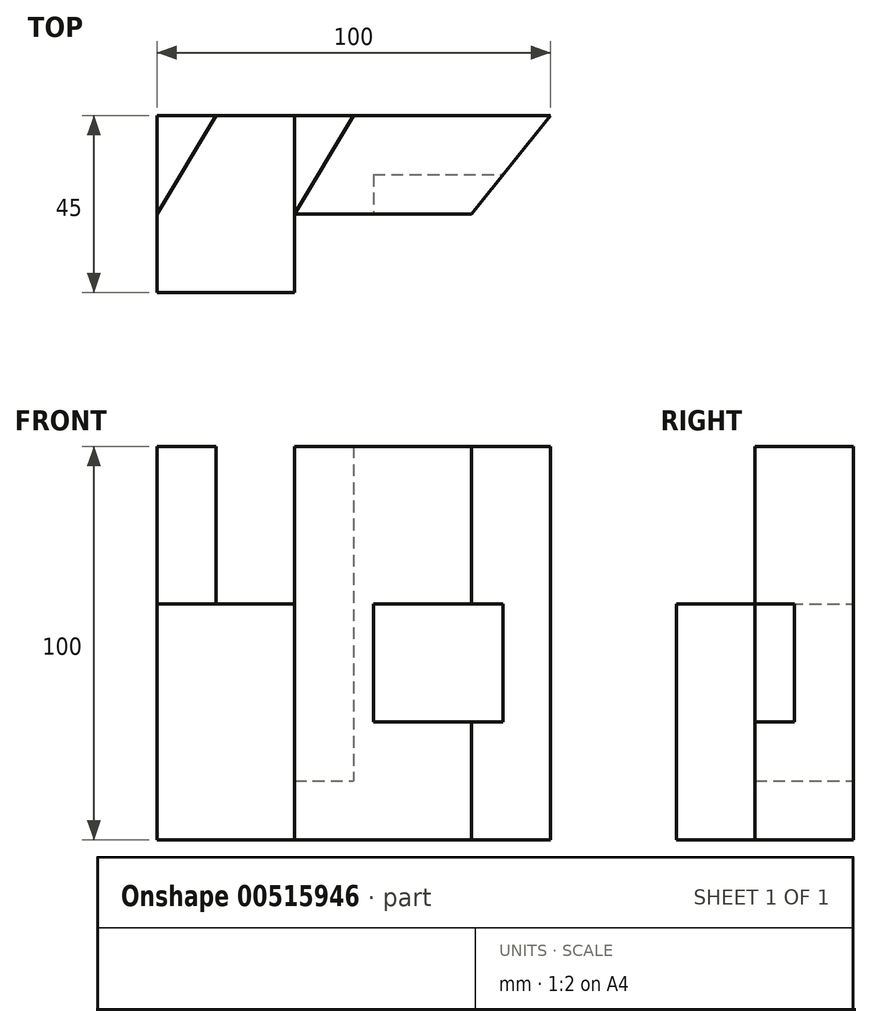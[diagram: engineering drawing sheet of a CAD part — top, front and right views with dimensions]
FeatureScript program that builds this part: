
annotation { "Feature Type Name" : "Feature", "Feature Type Description" : "" }
export const myFeature = defineFeature(function(context is Context, id is Id, definition is map)
    precondition{}
    {
        {
            var Q0;
            Q0=qCreatedBy(makeId("Top.planeOp"),FACE);
            var sketch = newSketch(context, id + "F0", { "sketchPlane" : qUnion([Q0])});
            skLineSegment(sketch, "E0.bottom", {"start": v(0, 0) * mm, "end": v(35, 0) * mm});
            skLineSegment(sketch, "E0.top", {"start": v(0, 45) * mm, "end": v(35, 45) * mm});
            skLineSegment(sketch, "E0.left", {"start": v(0, 0) * mm, "end": v(0, 45) * mm});
            skLineSegment(sketch, "E0.right", {"start": v(35, 0) * mm, "end": v(35, 45) * mm});
            skLineSegment(sketch, "E1.bottom", {"start": v(35, 45) * mm, "end": v(100, 45) * mm});
            skLineSegment(sketch, "E1.top", {"start": v(35, 20) * mm, "end": v(100, 20) * mm});
            skLineSegment(sketch, "E1.left", {"start": v(35, 45) * mm, "end": v(35, 20) * mm});
            skLineSegment(sketch, "E1.right", {"start": v(100, 45) * mm, "end": v(100, 20) * mm});
            skLineSegment(sketch, "E2", {"start": v(15, 45) * mm, "end": v(0, 20) * mm});
            skLineSegment(sketch, "E3", {"start": v(50, 45) * mm, "end": v(35, 20) * mm});
            skLineSegment(sketch, "E4", {"start": v(100, 45) * mm, "end": v(80, 20) * mm});
            skSolve(sketch);
        }
        {
            var Q0;
            {var subQ3=sQuery(id+"F0.wireOp",EDGE,"E2");Q0=makeQuery(id+"F0.imprint","IMPRINT",FACE,{"disambiguationData":[TD([[makeQuery(id+"F0.imprint","IMPRINT",EDGE,{"derivedFrom":subQ3}),-1.0]])]});}
            var Q1;
            {var subQ1=sQuery(id+"F0.wireOp",EDGE,"E0.bottom");Q1=makeQuery(id+"F0.imprint","IMPRINT",FACE,{"disambiguationData":[TD([[makeQuery(id+"F0.imprint","IMPRINT",EDGE,{"derivedFrom":subQ1}),1.0]])]});}
            extrude(context, id + "F1", {"entities" : qUnion([Q0, Q1]), "depth" : 60 * mm, "offsetDistance" : 25 * mm});
        }
        {
            var Q0;
            {var subQ3=sQuery(id+"F0.wireOp",EDGE,"E3");Q0=makeQuery(id+"F0.imprint","IMPRINT",FACE,{"disambiguationData":[TD([[makeQuery(id+"F0.imprint","IMPRINT",EDGE,{"derivedFrom":subQ3}),-1.0]])]});}
            extrude(context, id + "F2", {"entities" : qUnion([Q0]), "operationType" : NewBodyOperationType.ADD, "depth" : 15 * mm, "offsetDistance" : 25 * mm});
        }
        {
            var Q0;
            {var subQ3=sQuery(id+"F0.wireOp",EDGE,"E2");Q0=makeQuery(id+"F0.imprint","IMPRINT",FACE,{"disambiguationData":[TD([[makeQuery(id+"F0.imprint","IMPRINT",EDGE,{"derivedFrom":subQ3}),-1.0]])]});}
            extrude(context, id + "F3", {"entities" : qUnion([Q0]), "operationType" : NewBodyOperationType.ADD, "depth" : 100 * mm, "offsetDistance" : 25 * mm});
        }
        {
            var Q0;
            {var subQ0=sQuery(id+"F0.wireOp",EDGE,"E3");Q0=makeQuery(id+"F0.imprint","IMPRINT",FACE,{"disambiguationData":[TD([[makeQuery(id+"F0.imprint","IMPRINT",EDGE,{"derivedFrom":subQ0}),1.0]])]});}
            extrude(context, id + "F4", {"entities" : qUnion([Q0]), "operationType" : NewBodyOperationType.ADD, "depth" : 100 * mm, "offsetDistance" : 25 * mm});
        }
        {
            var Q0;
            Q0=makeQuery(id+"F4.opExtrude","SWEPT_FACE",FACE,{"disambiguationData":[OSD([sQuery(id+"F0.wireOp",EDGE,"E1.top")])]});
            var sketch = newSketch(context, id + "F5", { "sketchPlane" : qUnion([Q0])});
            skLineSegment(sketch, "E5.bottom", {"start": v(55, 60) * mm, "end": v(104.25, 60) * mm});
            skLineSegment(sketch, "E5.top", {"start": v(55, 30) * mm, "end": v(104.25, 30) * mm});
            skLineSegment(sketch, "E5.left", {"start": v(55, 60) * mm, "end": v(55, 30) * mm});
            skLineSegment(sketch, "E5.right", {"start": v(104.25, 60) * mm, "end": v(104.25, 30) * mm});
            skSolve(sketch);
        }
        {
            var Q0;
            Q0 = qSketchRegion(id + "F5", true);
            extrude(context, id + "F6", {"entities" : qUnion([Q0]), "operationType" : NewBodyOperationType.REMOVE, "oppositeDirection" : true, "depth" : 10 * mm, "offsetDistance" : 25 * mm});
        }
    });
